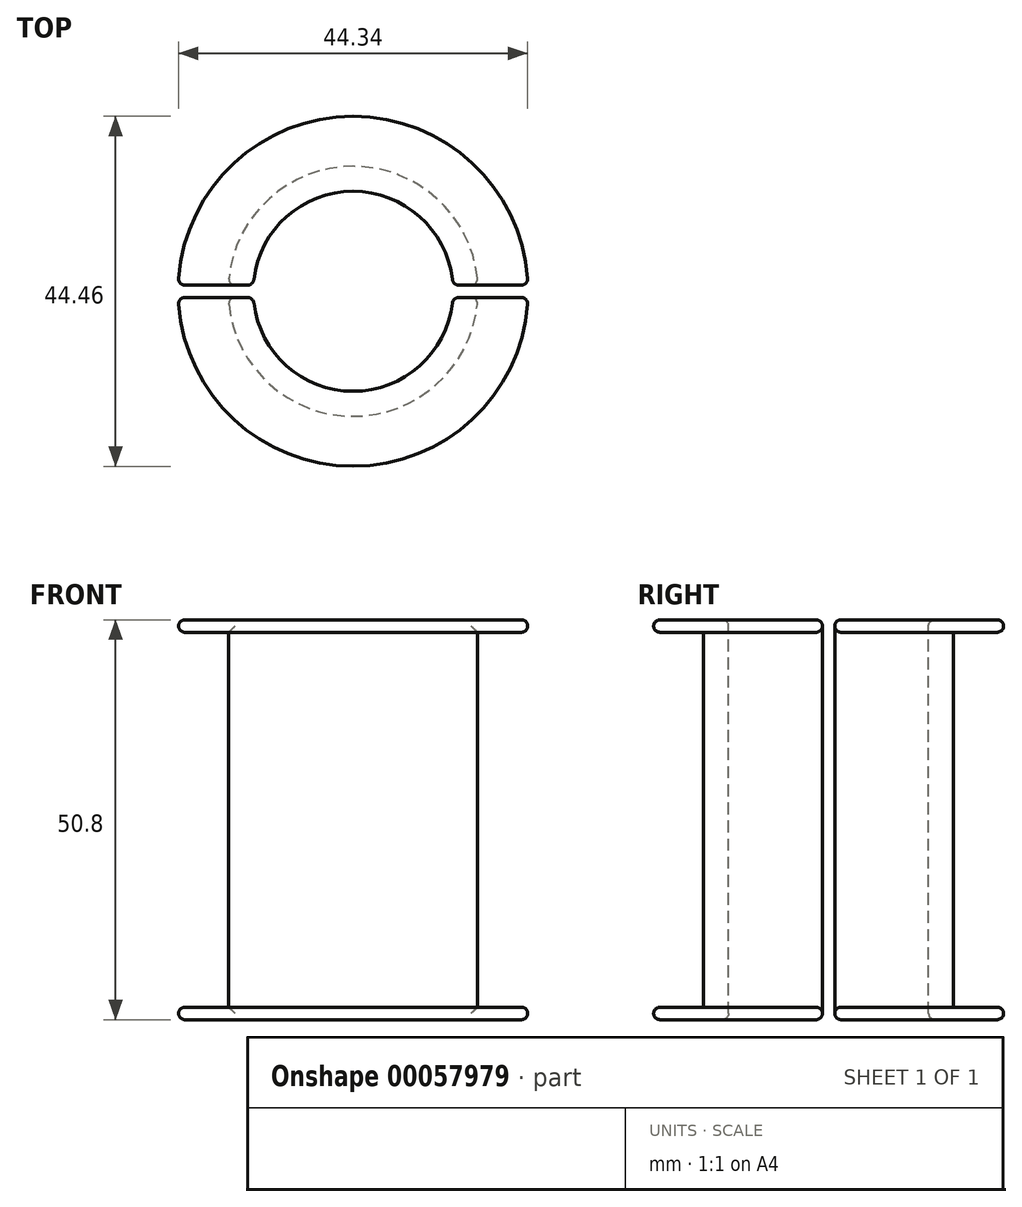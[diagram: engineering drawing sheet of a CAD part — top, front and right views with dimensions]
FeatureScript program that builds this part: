
annotation { "Feature Type Name" : "Feature", "Feature Type Description" : "" }
export const myFeature = defineFeature(function(context is Context, id is Id, definition is map)
    precondition{}
    {
        {
            var Q0;
            Q0=qCreatedBy(makeId("Right.planeOp"),FACE);
            var sketch = newSketch(context, id + "F0", { "sketchPlane" : qUnion([Q0])});
            skLineSegment(sketch, "E0", {"start": v(0, 25.4) * mm, "end": v(0, -25.4) * mm, "construction": true});
            skLineSegment(sketch, "E1", {"start": v(-13.49, 25.4) * mm, "end": v(-21.44, 25.4) * mm});
            skLineSegment(sketch, "E2", {"start": v(-22.23, 24.61) * mm, "end": v(-22.23, 24.6) * mm});
            skLineSegment(sketch, "E3", {"start": v(-21.44, 23.81) * mm, "end": v(-15.88, 23.81) * mm});
            skLineSegment(sketch, "E4", {"start": v(-15.88, 23.81) * mm, "end": v(-15.87, -23.81) * mm});
            skLineSegment(sketch, "E5", {"start": v(-15.87, -23.81) * mm, "end": v(-21.44, -23.81) * mm});
            skLineSegment(sketch, "E6", {"start": v(-22.22, -24.6) * mm, "end": v(-22.22, -24.61) * mm});
            skLineSegment(sketch, "E7", {"start": v(-21.44, -25.4) * mm, "end": v(-13.49, -25.4) * mm});
            skLineSegment(sketch, "E8", {"start": v(-12.7, 24.61) * mm, "end": v(-12.7, -24.61) * mm});
            skPoint(sketch, "E9.visualSharp", {"position": v(-12.7, 25.4) * mm});
            skArc(sketch, "E9.filletArc", {"start": v(-12.7, 24.61) * mm, "mid": v(-12.93, 25.17) * mm, "end": v(-13.49, 25.4) * mm});
            skPoint(sketch, "E10.visualSharp", {"position": v(-22.23, 25.4) * mm});
            skArc(sketch, "E10.filletArc", {"start": v(-21.44, 25.4) * mm, "mid": v(-22, 25.17) * mm, "end": v(-22.23, 24.61) * mm});
            skPoint(sketch, "E11.visualSharp", {"position": v(-22.23, 23.81) * mm});
            skArc(sketch, "E11.filletArc", {"start": v(-22.23, 24.6) * mm, "mid": v(-22, 24.04) * mm, "end": v(-21.44, 23.81) * mm});
            skPoint(sketch, "E12.visualSharp", {"position": v(-12.7, -25.4) * mm});
            skArc(sketch, "E12.filletArc", {"start": v(-13.49, -25.4) * mm, "mid": v(-12.93, -25.17) * mm, "end": v(-12.7, -24.61) * mm});
            skPoint(sketch, "E13.visualSharp", {"position": v(-22.22, -25.4) * mm});
            skArc(sketch, "E13.filletArc", {"start": v(-22.22, -24.61) * mm, "mid": v(-22, -25.17) * mm, "end": v(-21.44, -25.4) * mm});
            skPoint(sketch, "E14.visualSharp", {"position": v(-22.22, -23.81) * mm});
            skArc(sketch, "E14.filletArc", {"start": v(-21.44, -23.81) * mm, "mid": v(-22, -24.04) * mm, "end": v(-22.22, -24.6) * mm});
            skSolve(sketch);
        }
        {
            var Q0;
            Q0=makeQuery(id+"F0.imprint","IMPRINT",FACE,{"disambiguationData":[TD([[makeQuery(id+"F0.imprint","IMPRINT",EDGE,{"derivedFrom":sQuery(id+"F0.wireOp",EDGE,"E1")}),1.0]])]});
            var Q1;
            Q1=sQuery(id+"F0.wireOp",EDGE,"E0");
            revolve(context, id + "F1", {"entities" : qUnion([Q0]), "axis" : qUnion([Q1]), "revolveType" : RevolveType.FULL});
        }
        {
            var Q0;
            Q0=qCreatedBy(makeId("Top.planeOp"),FACE);
            var sketch = newSketch(context, id + "F2", { "sketchPlane" : qUnion([Q0])});
            skLineSegment(sketch, "E15.rect.bottom", {"start": v(-25.4, 0.79) * mm, "end": v(25.4, 0.79) * mm});
            skLineSegment(sketch, "E15.rect.top", {"start": v(-25.4, -0.79) * mm, "end": v(25.4, -0.79) * mm});
            skLineSegment(sketch, "E15.rect.left", {"start": v(-25.4, 0.79) * mm, "end": v(-25.4, -0.79) * mm});
            skLineSegment(sketch, "E15.rect.right", {"start": v(25.4, 0.79) * mm, "end": v(25.4, -0.79) * mm});
            skPoint(sketch, "E15.rect.middle", {"position": v(0, 0) * mm});
            skSolve(sketch);
        }
        {
            var Q0;
            Q0 = qSketchRegion(id + "F2", true);
            extrude(context, id + "F3", {"entities" : qUnion([Q0]), "operationType" : NewBodyOperationType.REMOVE, "endBound" : BoundingType.SYMMETRIC, "oppositeDirection" : true, "depth" : 50.8 * mm});
        }
        {
            var Q0;
            Q0=qCreatedBy(makeId("Front.planeOp"),FACE);
            var sketch = newSketch(context, id + "F4", { "sketchPlane" : qUnion([Q0])});
            skLineSegment(sketch, "E16.rect.bottom", {"start": v(25.4, 1.59) * mm, "end": v(-25.4, 1.59) * mm});
            skLineSegment(sketch, "E16.rect.top", {"start": v(25.4, -1.59) * mm, "end": v(-25.4, -1.59) * mm});
            skLineSegment(sketch, "E16.rect.left", {"start": v(25.4, 1.59) * mm, "end": v(25.4, -1.59) * mm});
            skLineSegment(sketch, "E16.rect.right", {"start": v(-25.4, 1.59) * mm, "end": v(-25.4, -1.59) * mm});
            skPoint(sketch, "E16.rect.middle", {"position": v(0, 0) * mm});
            skSolve(sketch);
        }
        {
            var Q0;
            Q0=makeQuery(id+"F3.boolean.opBoolean","COPY",FACE,{"disambiguationData":[OD(1.0)],"derivedFrom":makeQuery(id+"F3.opExtrude","SWEPT_FACE",FACE,{"disambiguationData":[OSD([sQuery(id+"F2.wireOp",EDGE,"E15.rect.bottom")])]})});
            var Q1;
            Q1=makeQuery(id+"F3.boolean.opBoolean","COPY",FACE,{"disambiguationData":[OD(0.0)],"derivedFrom":makeQuery(id+"F3.opExtrude","SWEPT_FACE",FACE,{"disambiguationData":[OSD([sQuery(id+"F2.wireOp",EDGE,"E15.rect.bottom")])]})});
            var Q2;
            Q2=makeQuery(id+"F3.boolean.opBoolean","COPY",FACE,{"disambiguationData":[OD(1.0)],"derivedFrom":makeQuery(id+"F3.opExtrude","SWEPT_FACE",FACE,{"disambiguationData":[OSD([sQuery(id+"F2.wireOp",EDGE,"E15.rect.top")])]})});
            var Q3;
            Q3=makeQuery(id+"F3.boolean.opBoolean","COPY",FACE,{"disambiguationData":[OD(0.0)],"derivedFrom":makeQuery(id+"F3.opExtrude","SWEPT_FACE",FACE,{"disambiguationData":[OSD([sQuery(id+"F2.wireOp",EDGE,"E15.rect.top")])]})});
            fillet(context, id + "F5", {"entities" : qUnion([Q0, Q1, Q2, Q3]), "radius" : 0.79 * mm, "tangentPropagation" : true, "allowEdgeOverflow" : false});
        }
    });
